# Revit family: Pablo-IP_40-Transparent_Door-syst-NoHosted-IT-en
name_source: partatom
category: Electrical Equipment
units: mm (PartAtom-declared; Revit-internal decimal feet)

## family parameters
Always vertical = Yes
Cut with Voids When Loaded = No
Panel Configuration = Two Columns, Circuits Across
Part Type = Panelboard
Room Calculation Point = No
Round Connector Dimension = Use Diameter
Shared = No
Work Plane-Based = Yes

## types (13) — shared parameters
Default Elevation = 1219 mm
EF000003 - Mounting method = EV000384 - Surface mounted (plaster)
EF000118 - With mounting plate = No
EF000339 - Type of cover = EV004216 - Door
EF001062 - EMC-version = No
EF001088 - Extension possible = No
EF001134 - DIN-rail = Yes
EF001596 - Material housing = EV000139 - Plastic
EF004462 - Type of closure = EV000154 - Other
EF005474 - Degree of protection (IP) = EV006415 - IP40
EF006244 - Transparent cover/door = Yes
EF006306 - With lock = No
EF015776 - Earthing terminal block = No
EF015777 - Neutral terminal block = No
EF015941 - Signal passing door = No
HG000001 - Number of columns = 1
HG000002 - With door or cover = Yes
HG000003 - Range = Pablo
HG000005 - Thickness = 3 mm  [stored 0.00984252 ft]
HG000006 - Flush mounted = No
HG000009 - Double swing door = No
HG000010 - Asymmetric doors = No
HG000011 - Empty rows from bottom = No
Manufacturer = Hager
Type Comments = Pablo
zero-valued in all types: EF000218 - Built-in depth, EF000332 - Built-in height, EF000846 - Built-in width, HG000007 - Number of empty columns, HG000008 - Number of empty rows

## per-type parameters (varying)
| type | EF000007 - Colour | EF000008 - Width | EF000040 - Height | EF000049 - Depth | EF000116 - RAL-number | EF000266 - Number of rows | EF001131 - Internal depth | EF002950 - Width in number of modular spacings | EF009212 - Cover model | HG000004 - Manufacturer reference | Model |
| Surface mounted IP40 W110 H140 D86 4 Modular spacings - B04000 | EV000270 - Grey | 110 mm  [stored 0.360892 ft] | 140 mm  [stored 0.459318 ft] | 86 mm  [stored 0.282152 ft] | 7035 | 1 | 86 mm  [stored 0.282152 ft] | 4 | EV009916 - With notch | B04000 | B04000 |
| Surface mounted IP40 W210 H200 D103 8 Modular spacings - B04002 | EV000270 - Grey | 210 mm  [stored 0.688976 ft] | 200 mm  [stored 0.656168 ft] | 103 mm  [stored 0.337927 ft] | 7035 | 1 | 103 mm  [stored 0.337927 ft] | 8 | EV009916 - With notch | B04002 | B04002 |
| Surface mounted IP40 W210 H200 D103 8 Modular spacings - B04083 | EV000270 - Grey | 210 mm  [stored 0.688976 ft] | 200 mm  [stored 0.656168 ft] | 103 mm  [stored 0.337927 ft] | 9001 | 1 | 48 mm  [stored 0.15748 ft] | 8 | EV000116 - Closed | B04083 | B04083 |
| Surface mounted IP40 W300 H250 D113 12 Modular spacings - B04010 | EV000270 - Grey | 300 mm | 250 mm  [stored 0.82021 ft] | 113 mm  [stored 0.370735 ft] | 7035 | 1 | 113 mm  [stored 0.370735 ft] | 12 | EV009916 - With notch | B04010 | B04010 |
| Surface mounted IP40 W300 H250 D113 12 Modular spacings - B04084 | EV000202 - White | 300 mm | 250 mm  [stored 0.82021 ft] | 113 mm  [stored 0.370735 ft] | 9001 | 1 | 48 mm  [stored 0.15748 ft] | 12 | EV000116 - Closed | B04084 | B04084 |
| Surface mounted IP40 W300 H400 D113 12 Modular spacings - B04020 | EV000270 - Grey | 300 mm | 400 mm  [stored 1.31234 ft] | 113 mm  [stored 0.370735 ft] | 7035 | 2 | 113 mm  [stored 0.370735 ft] | 12 | EV009916 - With notch | B04020 | B04020 |
| Surface mounted IP40 W300 H400 D113 12 Modular spacings - B04086 | EV000202 - White | 300 mm | 400 mm  [stored 1.31234 ft] | 113 mm  [stored 0.370735 ft] | 9001 | 2 | 48 mm  [stored 0.15748 ft] | 12 | EV000116 - Closed | B04086 | B04086 |
| Surface mounted IP40 W408 H275 D137 18 Modular spacings - B04011 | EV000270 - Grey | 408 mm | 275 mm | 137 mm  [stored 0.449475 ft] | 7035 | 1 | 137 mm  [stored 0.449475 ft] | 18 | EV009916 - With notch | B04011 | B04011 |
| Surface mounted IP40 W408 H275 D137 18 Modular spacings - B04085 | EV000202 - White | 408 mm | 275 mm | 137 mm  [stored 0.449475 ft] | 9001 | 1 | 48 mm  [stored 0.15748 ft] | 18 | EV000116 - Closed | B04085 | B04085 |
| Surface mounted IP40 W408 H450 D137 18 Modular spacings - B04021 | EV000270 - Grey | 408 mm | 450 mm  [stored 1.47638 ft] | 137 mm  [stored 0.449475 ft] | 7035 | 2 | 137 mm  [stored 0.449475 ft] | 18 | EV009916 - With notch | B04021 | B04021 |
| Surface mounted IP40 W408 H450 D137 18 Modular spacings - B04089 | EV000270 - Grey | 408 mm | 450 mm  [stored 1.47638 ft] | 137 mm  [stored 0.449475 ft] | 9001 | 2 | 48 mm  [stored 0.15748 ft] | 18 | EV000116 - Closed | B04089 | B04089 |
| Surface mounted IP40 W408 H625 D137 18 Modular spacings - B04022 | EV000270 - Grey | 408 mm | 625 mm  [stored 2.05052 ft] | 137 mm  [stored 0.449475 ft] | 7035 | 3 | 137 mm  [stored 0.449475 ft] | 18 | EV009916 - With notch | B04022 | B04022 |
| Surface mounted IP40 W408 H625 D137 18 Modular spacings - B04090 | EV000202 - White | 408 mm | 625 mm  [stored 2.05052 ft] | 137 mm  [stored 0.449475 ft] | 9001 | 3 | 48 mm  [stored 0.15748 ft] | 18 | EV000116 - Closed | B04090 | B04090 |

note: [stored X ft] marks values corroborated as IEEE doubles in the binary element streams (Revit-internal decimal feet)

## geometry (parser evidence)
native form markers: Sweep x16
no freeform markers — native parametric forms only
